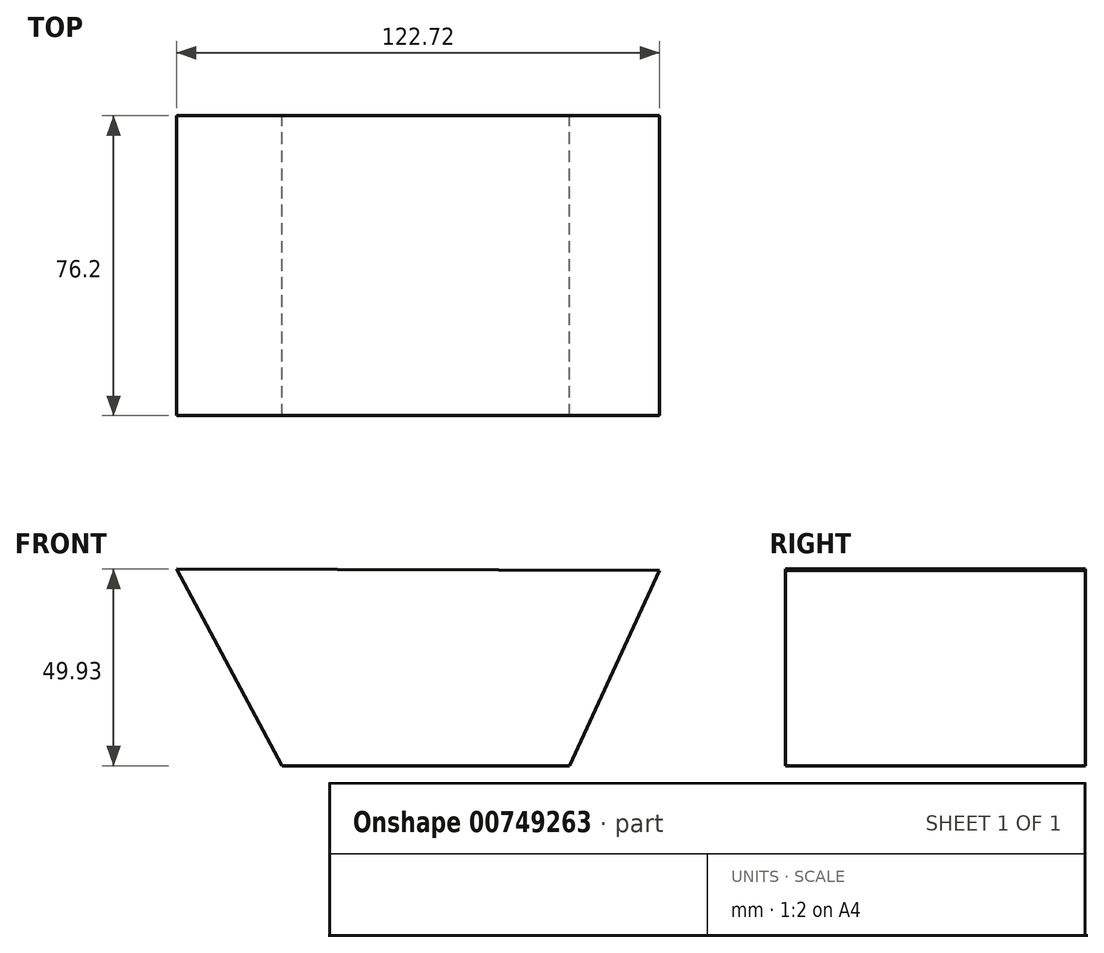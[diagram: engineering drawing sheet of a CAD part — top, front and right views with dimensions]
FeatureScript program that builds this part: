
annotation { "Feature Type Name" : "Feature", "Feature Type Description" : "" }
export const myFeature = defineFeature(function(context is Context, id is Id, definition is map)
    precondition{}
    {
        {
            var Q0;
            Q0=qCreatedBy(makeId("Front.planeOp"),FACE);
            var sketch = newSketch(context, id + "F0", { "sketchPlane" : qUnion([Q0])});
            skLineSegment(sketch, "E0", {"start": v(-65.12, 24.21) * mm, "end": v(-38.35, -25.72) * mm});
            skLineSegment(sketch, "E1", {"start": v(-38.35, -25.72) * mm, "end": v(34.74, -25.72) * mm});
            skLineSegment(sketch, "E2", {"start": v(34.74, -25.72) * mm, "end": v(57.6, 23.91) * mm});
            skLineSegment(sketch, "E3", {"start": v(57.6, 23.91) * mm, "end": v(-65.12, 24.21) * mm});
            skSolve(sketch);
        }
        {
            var Q0;
            Q0 = qSketchRegion(id + "F0", true);
            extrude(context, id + "F1", {"entities" : qUnion([Q0]), "depth" : 76.2 * mm, "offsetDistance" : 25.4 * mm});
        }
    });
